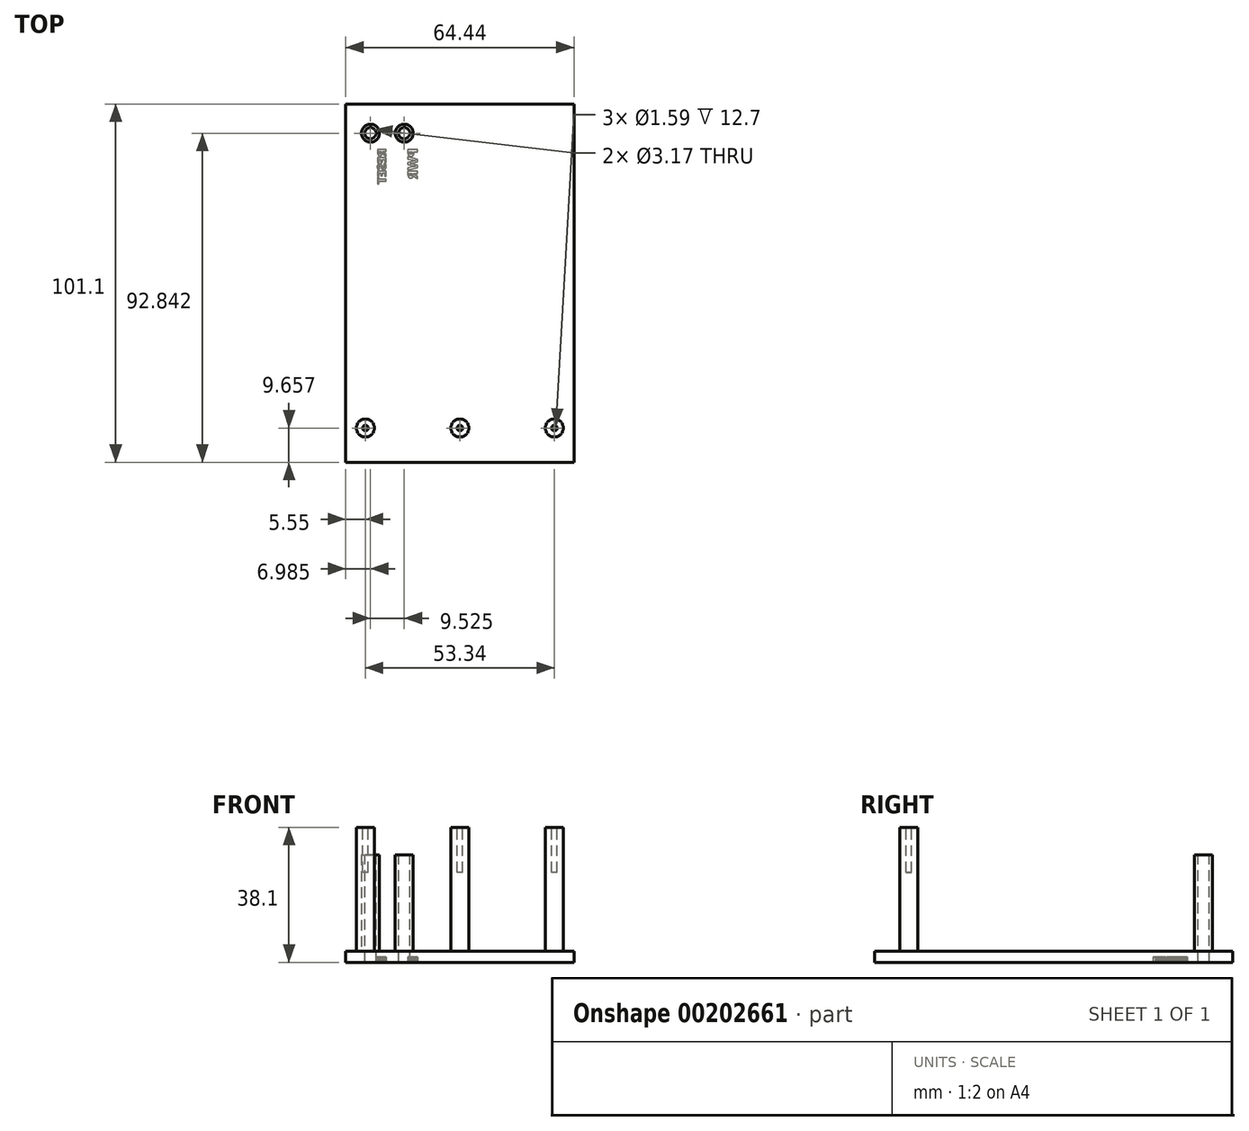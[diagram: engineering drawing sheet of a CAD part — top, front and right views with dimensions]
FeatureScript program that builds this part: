
annotation { "Feature Type Name" : "Feature", "Feature Type Description" : "" }
export const myFeature = defineFeature(function(context is Context, id is Id, definition is map)
    precondition{}
    {
        {
            var Q0;
            Q0=qCreatedBy(makeId("Top.planeOp"),FACE);
            var sketch = newSketch(context, id + "F0", { "sketchPlane" : qUnion([Q0])});
            skLineSegment(sketch, "E0.bottom", {"start": v(-64.44, 104.27) * mm, "end": v(0, 104.27) * mm});
            skLineSegment(sketch, "E0.top", {"start": v(-64.44, 0) * mm, "end": v(0, 0) * mm});
            skLineSegment(sketch, "E0.left", {"start": v(-64.44, 104.27) * mm, "end": v(-64.44, 0) * mm});
            skLineSegment(sketch, "E0.right", {"start": v(0, 104.27) * mm, "end": v(0, 0) * mm});
            skSolve(sketch);
        }
        {
            var Q0;
            Q0 = qSketchRegion(id + "F0", true);
            extrude(context, id + "F1", {"entities" : qUnion([Q0]), "depth" : 3.17 * mm});
        }
        {
            var Q0;
            Q0=makeQuery(id+"F1.opExtrude","CAP_FACE",FACE,{"disambiguationData":[OSD([sQuery(id+"F0.wireOp",EDGE,"E0.bottom"),sQuery(id+"F0.wireOp",EDGE,"E0.top"),sQuery(id+"F0.wireOp",EDGE,"E0.left"),sQuery(id+"F0.wireOp",EDGE,"E0.right")])],"isStart":false});
            var sketch = newSketch(context, id + "F2", { "sketchPlane" : qUnion([Q0])});
            skLineSegment(sketch, "E1.bottom", {"start": v(-64.44, 0) * mm, "end": v(0, 0) * mm});
            skLineSegment(sketch, "E1.top", {"start": v(-64.44, 3.17) * mm, "end": v(0, 3.17) * mm});
            skLineSegment(sketch, "E1.left", {"start": v(-64.44, 0) * mm, "end": v(-64.44, 3.17) * mm});
            skLineSegment(sketch, "E1.right", {"start": v(0, 0) * mm, "end": v(0, 3.17) * mm});
            skSolve(sketch);
        }
        {
            var Q0;
            Q0 = qSketchRegion(id + "F2", true);
            extrude(context, id + "F3", {"entities" : qUnion([Q0]), "operationType" : NewBodyOperationType.ADD, "depth" : 34.92 * mm});
        }
        {
            var Q0;
            Q0=makeQuery(id+"F1.opExtrude","CAP_FACE",FACE,{"disambiguationData":[OSD([sQuery(id+"F0.wireOp",EDGE,"E0.bottom"),sQuery(id+"F0.wireOp",EDGE,"E0.top"),sQuery(id+"F0.wireOp",EDGE,"E0.left"),sQuery(id+"F0.wireOp",EDGE,"E0.right")])],"isStart":false});
            var sketch = newSketch(context, id + "F4", { "sketchPlane" : qUnion([Q0])});
            skCircle(sketch, "E2", {"center": v(-57.45, 96.01) * mm, "radius": 1.59 * mm});
            skCircle(sketch, "E3", {"center": v(-47.93, 96.01) * mm, "radius": 1.59 * mm});
            skSolve(sketch);
        }
        {
            var Q0;
            Q0 = qSketchRegion(id + "F4", true);
            extrude(context, id + "F5", {"entities" : qUnion([Q0]), "operationType" : NewBodyOperationType.REMOVE, "endBound" : BoundingType.THROUGH_ALL, "oppositeDirection" : true, "depth" : 25.4 * mm});
        }
        {
            var Q0;
            Q0=makeQuery(id+"F1.opExtrude","CAP_FACE",FACE,{"disambiguationData":[OSD([sQuery(id+"F0.wireOp",EDGE,"E0.bottom"),sQuery(id+"F0.wireOp",EDGE,"E0.top"),sQuery(id+"F0.wireOp",EDGE,"E0.left"),sQuery(id+"F0.wireOp",EDGE,"E0.right")])],"isStart":false});
            var sketch = newSketch(context, id + "F6", { "sketchPlane" : qUnion([Q0])});
            skCircle(sketch, "E4", {"center": v(-57.45, 96.01) * mm, "radius": 2.54 * mm});
            skCircle(sketch, "E5", {"center": v(-47.93, 96.01) * mm, "radius": 2.54 * mm});
            skCircle(sketch, "E6", {"center": v(-57.45, 96.01) * mm, "radius": 1.59 * mm});
            skCircle(sketch, "E7", {"center": v(-47.93, 96.01) * mm, "radius": 1.59 * mm});
            skSolve(sketch);
        }
        {
            var Q0;
            Q0 = qSketchRegion(id + "F6", true);
            extrude(context, id + "F7", {"entities" : qUnion([Q0]), "operationType" : NewBodyOperationType.ADD, "depth" : 27.18 * mm});
        }
        {
            var Q0;
            Q0=makeQuery(id+"F3.boolean.opBoolean","MERGE",FACE,{"derivedFrom":[makeQuery(id+"F1.opExtrude","SWEPT_FACE",FACE,{"disambiguationData":[OSD([sQuery(id+"F0.wireOp",EDGE,"E0.right")])]}),makeQuery(id+"F3.opExtrude","SWEPT_FACE",FACE,{"disambiguationData":[OSD([sQuery(id+"F2.wireOp",EDGE,"E1.right")])]})]});
            var sketch = newSketch(context, id + "F8", { "sketchPlane" : qUnion([Q0])});
            skLineSegment(sketch, "E8.bottom", {"start": v(2.16, 0) * mm, "end": v(3.17, 0) * mm});
            skLineSegment(sketch, "E8.top", {"start": v(2.16, 38.1) * mm, "end": v(3.17, 38.1) * mm});
            skLineSegment(sketch, "E8.left", {"start": v(2.16, 0) * mm, "end": v(2.16, 38.1) * mm});
            skLineSegment(sketch, "E8.right", {"start": v(3.17, 0) * mm, "end": v(3.17, 38.1) * mm});
            skSolve(sketch);
        }
        {
            var Q0;
            Q0 = qSketchRegion(id + "F8", true);
            extrude(context, id + "F9", {"entities" : qUnion([Q0]), "operationType" : NewBodyOperationType.ADD, "depth" : 1.59 * mm});
        }
        {
            var Q0;
            Q0=makeQuery(id+"F3.boolean.opBoolean","MERGE",FACE,{"derivedFrom":[makeQuery(id+"F1.opExtrude","SWEPT_FACE",FACE,{"disambiguationData":[OSD([sQuery(id+"F0.wireOp",EDGE,"E0.left")])]}),makeQuery(id+"F3.opExtrude","SWEPT_FACE",FACE,{"disambiguationData":[OSD([sQuery(id+"F2.wireOp",EDGE,"E1.left")])]})]});
            var sketch = newSketch(context, id + "F10", { "sketchPlane" : qUnion([Q0])});
            skLineSegment(sketch, "E9.bottom", {"start": v(-2.16, 0) * mm, "end": v(-3.17, 0) * mm});
            skLineSegment(sketch, "E9.top", {"start": v(-2.16, 38.1) * mm, "end": v(-3.18, 38.1) * mm});
            skLineSegment(sketch, "E9.left", {"start": v(-2.16, 0) * mm, "end": v(-2.16, 38.1) * mm});
            skLineSegment(sketch, "E9.right", {"start": v(-3.17, 0) * mm, "end": v(-3.18, 38.1) * mm});
            skSolve(sketch);
        }
        {
            var Q0;
            Q0 = qSketchRegion(id + "F10", true);
            extrude(context, id + "F11", {"entities" : qUnion([Q0]), "operationType" : NewBodyOperationType.ADD, "depth" : 1.59 * mm});
        }
        {
            var Q0;
            Q0=makeQuery(id+"F3.boolean.opBoolean","MERGE",FACE,{"derivedFrom":[makeQuery(id+"F1.opExtrude","SWEPT_FACE",FACE,{"disambiguationData":[OSD([sQuery(id+"F0.wireOp",EDGE,"E0.top")])]}),makeQuery(id+"F3.opExtrude","SWEPT_FACE",FACE,{"disambiguationData":[OSD([sQuery(id+"F2.wireOp",EDGE,"E1.bottom")])]})]});
            var sketch = newSketch(context, id + "F12", { "sketchPlane" : qUnion([Q0])});
            skLineSegment(sketch, "E10", {"start": v(-5, 4.7) * mm, "end": v(-24.82, 4.7) * mm});
            skLineSegment(sketch, "E11", {"start": v(-24.82, 4.7) * mm, "end": v(-23.42, 15.53) * mm});
            skLineSegment(sketch, "E12", {"start": v(-23.42, 15.53) * mm, "end": v(-6.4, 15.53) * mm});
            skLineSegment(sketch, "E13", {"start": v(-6.4, 15.53) * mm, "end": v(-5, 4.7) * mm});
            skLineSegment(sketch, "E14", {"start": v(0.5, 3.83) * mm, "end": v(-30.31, 3.83) * mm, "construction": true});
            skLineSegment(sketch, "E15", {"start": v(-30.31, 3.83) * mm, "end": v(-30.31, 16.4) * mm, "construction": true});
            skLineSegment(sketch, "E16", {"start": v(-30.31, 16.4) * mm, "end": v(0.5, 16.4) * mm, "construction": true});
            skLineSegment(sketch, "E17", {"start": v(0.5, 16.4) * mm, "end": v(0.5, 3.83) * mm, "construction": true});
            skLineSegment(sketch, "E18", {"start": v(-14.9, 4.7) * mm, "end": v(-14.9, 15.53) * mm, "construction": true});
            skLineSegment(sketch, "E19", {"start": v(-14.9, 10.12) * mm, "end": v(-30.31, 10.12) * mm, "construction": true});
            skLineSegment(sketch, "E20", {"start": v(-14.9, 10.12) * mm, "end": v(0.5, 10.12) * mm, "construction": true});
            skLineSegment(sketch, "E21", {"start": v(-5, 26.4) * mm, "end": v(-24.82, 26.4) * mm});
            skLineSegment(sketch, "E22", {"start": v(-24.82, 26.4) * mm, "end": v(-23.42, 37.23) * mm});
            skLineSegment(sketch, "E23", {"start": v(-23.42, 37.23) * mm, "end": v(-6.4, 37.23) * mm});
            skLineSegment(sketch, "E24", {"start": v(-6.4, 37.23) * mm, "end": v(-5, 26.4) * mm});
            skLineSegment(sketch, "E25", {"start": v(0.5, 25.53) * mm, "end": v(-30.31, 25.53) * mm, "construction": true});
            skLineSegment(sketch, "E26", {"start": v(-30.31, 25.53) * mm, "end": v(-30.31, 38.1) * mm, "construction": true});
            skLineSegment(sketch, "E27", {"start": v(-30.31, 38.1) * mm, "end": v(0.5, 38.1) * mm, "construction": true});
            skLineSegment(sketch, "E28", {"start": v(0.5, 38.1) * mm, "end": v(0.5, 25.53) * mm, "construction": true});
            skLineSegment(sketch, "E29", {"start": v(-14.9, 26.4) * mm, "end": v(-14.9, 37.23) * mm, "construction": true});
            skLineSegment(sketch, "E30", {"start": v(-14.9, 31.81) * mm, "end": v(-30.31, 31.81) * mm, "construction": true});
            skLineSegment(sketch, "E31", {"start": v(-14.9, 31.81) * mm, "end": v(0.5, 31.81) * mm, "construction": true});
            skLineSegment(sketch, "E32", {"start": v(-39.62, 4.7) * mm, "end": v(-59.44, 4.7) * mm});
            skLineSegment(sketch, "E33", {"start": v(-59.44, 4.7) * mm, "end": v(-58.04, 15.53) * mm});
            skLineSegment(sketch, "E34", {"start": v(-58.04, 15.53) * mm, "end": v(-41.02, 15.53) * mm});
            skLineSegment(sketch, "E35", {"start": v(-41.02, 15.53) * mm, "end": v(-39.62, 4.7) * mm});
            skLineSegment(sketch, "E36", {"start": v(-34.12, 3.83) * mm, "end": v(-64.94, 3.83) * mm, "construction": true});
            skLineSegment(sketch, "E37", {"start": v(-64.94, 3.83) * mm, "end": v(-64.94, 16.4) * mm, "construction": true});
            skLineSegment(sketch, "E38", {"start": v(-64.94, 16.4) * mm, "end": v(-34.12, 16.4) * mm, "construction": true});
            skLineSegment(sketch, "E39", {"start": v(-34.12, 16.4) * mm, "end": v(-34.12, 3.83) * mm, "construction": true});
            skLineSegment(sketch, "E40", {"start": v(-49.53, 4.7) * mm, "end": v(-49.53, 15.53) * mm, "construction": true});
            skLineSegment(sketch, "E41", {"start": v(-49.53, 10.12) * mm, "end": v(-64.94, 10.12) * mm, "construction": true});
            skLineSegment(sketch, "E42", {"start": v(-49.53, 10.12) * mm, "end": v(-34.12, 10.12) * mm, "construction": true});
            skLineSegment(sketch, "E43", {"start": v(-39.62, 26.4) * mm, "end": v(-59.44, 26.4) * mm});
            skLineSegment(sketch, "E44", {"start": v(-59.44, 26.4) * mm, "end": v(-58.04, 37.23) * mm});
            skLineSegment(sketch, "E45", {"start": v(-58.04, 37.23) * mm, "end": v(-41.02, 37.23) * mm});
            skLineSegment(sketch, "E46", {"start": v(-41.02, 37.23) * mm, "end": v(-39.62, 26.4) * mm});
            skLineSegment(sketch, "E47", {"start": v(-34.12, 25.53) * mm, "end": v(-64.94, 25.53) * mm, "construction": true});
            skLineSegment(sketch, "E48", {"start": v(-64.94, 25.53) * mm, "end": v(-64.94, 38.1) * mm, "construction": true});
            skLineSegment(sketch, "E49", {"start": v(-64.94, 38.1) * mm, "end": v(-34.12, 38.1) * mm, "construction": true});
            skLineSegment(sketch, "E50", {"start": v(-34.12, 38.1) * mm, "end": v(-34.12, 25.53) * mm, "construction": true});
            skLineSegment(sketch, "E51", {"start": v(-49.53, 26.4) * mm, "end": v(-49.53, 37.23) * mm, "construction": true});
            skLineSegment(sketch, "E52", {"start": v(-49.53, 31.81) * mm, "end": v(-64.94, 31.81) * mm, "construction": true});
            skLineSegment(sketch, "E53", {"start": v(-49.53, 31.81) * mm, "end": v(-34.12, 31.81) * mm, "construction": true});
            skCircle(sketch, "E54", {"center": v(-27.6, 10.12) * mm, "radius": 1.52 * mm});
            skCircle(sketch, "E55", {"center": v(-2.2, 10.12) * mm, "radius": 1.52 * mm});
            skCircle(sketch, "E56", {"center": v(-2.2, 31.81) * mm, "radius": 1.52 * mm});
            skCircle(sketch, "E57", {"center": v(-27.6, 31.81) * mm, "radius": 1.52 * mm});
            skCircle(sketch, "E58", {"center": v(-36.83, 31.81) * mm, "radius": 1.52 * mm});
            skCircle(sketch, "E59", {"center": v(-62.23, 31.81) * mm, "radius": 1.52 * mm});
            skCircle(sketch, "E60", {"center": v(-62.23, 10.12) * mm, "radius": 1.52 * mm});
            skCircle(sketch, "E61", {"center": v(-36.83, 10.12) * mm, "radius": 1.52 * mm});
            skLineSegment(sketch, "E62", {"start": v(-49.53, 28.23) * mm, "end": v(-64.44, 28.23) * mm, "construction": true});
            skLineSegment(sketch, "E63", {"start": v(-14.9, 28.05) * mm, "end": v(0, 28.05) * mm, "construction": true});
            skSolve(sketch);
        }
        {
            var Q0;
            Q0 = qSketchRegion(id + "F12", true);
            extrude(context, id + "F13", {"entities" : qUnion([Q0]), "operationType" : NewBodyOperationType.REMOVE, "endBound" : BoundingType.UP_TO_NEXT, "oppositeDirection" : true, "depth" : 25.4 * mm});
        }
        {
            var Q0;
            Q0=makeQuery(id+"F11.boolean.opBoolean","MERGE",FACE,{"derivedFrom":[makeQuery(id+"F9.boolean.opBoolean","MERGE",FACE,{"derivedFrom":[makeQuery(id+"F1.opExtrude","CAP_FACE",FACE,{"disambiguationData":[OSD([sQuery(id+"F0.wireOp",EDGE,"E0.bottom"),sQuery(id+"F0.wireOp",EDGE,"E0.top"),sQuery(id+"F0.wireOp",EDGE,"E0.left"),sQuery(id+"F0.wireOp",EDGE,"E0.right")])],"isStart":true}),makeQuery(id+"F9.opExtrude","SWEPT_FACE",FACE,{"disambiguationData":[OSD([sQuery(id+"F8.wireOp",EDGE,"E8.bottom")])]})]}),makeQuery(id+"F11.opExtrude","SWEPT_FACE",FACE,{"disambiguationData":[OSD([sQuery(id+"F10.wireOp",EDGE,"E9.bottom")])]})]});
            var sketch = newSketch(context, id + "F14", { "sketchPlane" : qUnion([Q0])});
            skText(sketch, "E64", { "text": "PWR", "fontName": "OpenSans-Bold.ttf"});
            skText(sketch, "E65", { "text": "RESET", "fontName": "OpenSans-Bold.ttf"});
            const initialGuessF14  = {"E64": [-0.04418, -0.09173, 0, 1, 0.00276], "E65": [-0.05306, -0.09173, 0, 1, 0.00248]};
            skSetInitialGuess(sketch, initialGuessF14);
            skSolve(sketch);
        }
        {
            var Q0;
            Q0 = qSketchRegion(id + "F14", true);
            extrude(context, id + "F15", {"entities" : qUnion([Q0]), "operationType" : NewBodyOperationType.REMOVE, "oppositeDirection" : true, "depth" : 1.52 * mm});
        }
        {
            var Q0;
            Q0=makeQuery(id+"F11.boolean.opBoolean","MERGE",FACE,{"derivedFrom":[makeQuery(id+"F9.boolean.opBoolean","MERGE",FACE,{"derivedFrom":[makeQuery(id+"F3.opExtrude","CAP_FACE",FACE,{"disambiguationData":[OSD([sQuery(id+"F2.wireOp",EDGE,"E1.bottom"),sQuery(id+"F2.wireOp",EDGE,"E1.top"),sQuery(id+"F2.wireOp",EDGE,"E1.left"),sQuery(id+"F2.wireOp",EDGE,"E1.right")])],"isStart":false}),makeQuery(id+"F9.opExtrude","SWEPT_FACE",FACE,{"disambiguationData":[OSD([sQuery(id+"F8.wireOp",EDGE,"E8.top")])]})]}),makeQuery(id+"F11.opExtrude","SWEPT_FACE",FACE,{"disambiguationData":[OSD([sQuery(id+"F10.wireOp",EDGE,"E9.top")])]})]});
            var sketch = newSketch(context, id + "F16", { "sketchPlane" : qUnion([Q0])});
            skLineSegment(sketch, "E66.bottom", {"start": v(1.59, 3.17) * mm, "end": v(-66.03, 3.17) * mm});
            skLineSegment(sketch, "E66.top", {"start": v(1.59, 0) * mm, "end": v(-66.03, 0) * mm});
            skLineSegment(sketch, "E66.left", {"start": v(1.59, 3.17) * mm, "end": v(1.59, 0) * mm});
            skLineSegment(sketch, "E66.right", {"start": v(-66.03, 3.17) * mm, "end": v(-66.03, 0) * mm});
            skSolve(sketch);
        }
        {
            var Q0;
            Q0 = qSketchRegion(id + "F16", true);
            extrude(context, id + "F17", {"entities" : qUnion([Q0]), "operationType" : NewBodyOperationType.REMOVE, "endBound" : BoundingType.THROUGH_ALL, "oppositeDirection" : true, "depth" : 25.4 * mm});
        }
        {
            var Q0;
            Q0=makeQuery(id+"F1.opExtrude","CAP_FACE",FACE,{"disambiguationData":[OSD([sQuery(id+"F0.wireOp",EDGE,"E0.bottom"),sQuery(id+"F0.wireOp",EDGE,"E0.top"),sQuery(id+"F0.wireOp",EDGE,"E0.left"),sQuery(id+"F0.wireOp",EDGE,"E0.right")])],"isStart":false});
            var sketch = newSketch(context, id + "F18", { "sketchPlane" : qUnion([Q0])});
            skCircle(sketch, "E67", {"center": v(-32.22, 12.83) * mm, "radius": 2.54 * mm});
            skCircle(sketch, "E68", {"center": v(-58.89, 12.83) * mm, "radius": 2.54 * mm});
            skCircle(sketch, "E69", {"center": v(-5.55, 12.83) * mm, "radius": 2.54 * mm});
            skLineSegment(sketch, "E70", {"start": v(0, 3.17) * mm, "end": v(-64.44, 3.17) * mm, "construction": true});
            skLineSegment(sketch, "E71", {"start": v(-32.22, 3.17) * mm, "end": v(-32.22, 12.83) * mm, "construction": true});
            skSolve(sketch);
        }
        {
            var Q0;
            Q0 = qSketchRegion(id + "F18", true);
            extrude(context, id + "F19", {"entities" : qUnion([Q0]), "operationType" : NewBodyOperationType.ADD, "depth" : 34.92 * mm});
        }
        {
            var Q0;
            Q0=makeQuery(id+"F19.opExtrude","CAP_FACE",FACE,{"disambiguationData":[OSD([sQuery(id+"F18.wireOp",EDGE,"E69")])],"isStart":false});
            var sketch = newSketch(context, id + "F20", { "sketchPlane" : qUnion([Q0])});
            skCircle(sketch, "E72", {"center": v(-5.55, 12.83) * mm, "radius": 0.8 * mm});
            skCircle(sketch, "E73", {"center": v(-32.22, 12.83) * mm, "radius": 0.8 * mm});
            skCircle(sketch, "E74", {"center": v(-58.89, 12.83) * mm, "radius": 0.8 * mm});
            skSolve(sketch);
        }
        {
            var Q0;
            Q0 = qSketchRegion(id + "F20", true);
            extrude(context, id + "F21", {"entities" : qUnion([Q0]), "operationType" : NewBodyOperationType.REMOVE, "oppositeDirection" : true, "depth" : 12.7 * mm});
        }
    });
